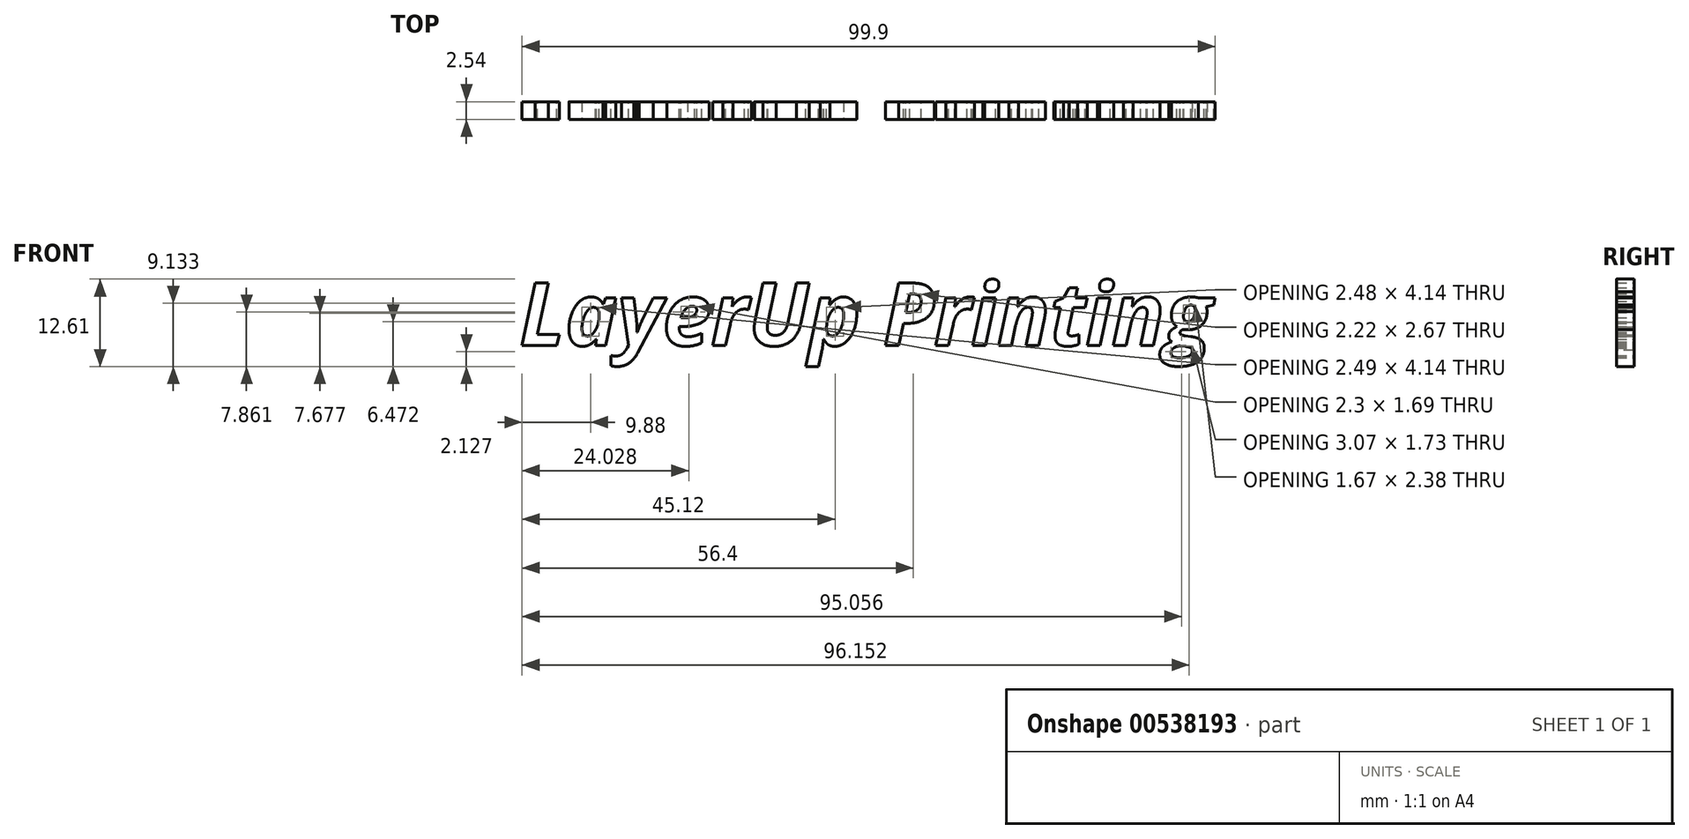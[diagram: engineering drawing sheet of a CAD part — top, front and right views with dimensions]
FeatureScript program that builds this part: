
annotation { "Feature Type Name" : "Feature", "Feature Type Description" : "" }
export const myFeature = defineFeature(function(context is Context, id is Id, definition is map)
    precondition{}
    {
        {
            var Q0;
            Q0=qCreatedBy(makeId("Front.planeOp"),FACE);
            var sketch = newSketch(context, id + "F0", { "sketchPlane" : qUnion([Q0])});
            skText(sketch, "E0", { "text": "LayerUp Printing", "fontName": "OpenSans-BoldItalic.ttf"});
            const initialGuessF0  = {"E0": [-0.06295, 0.01792, 1, 0, 0.00908]};
            skSetInitialGuess(sketch, initialGuessF0);
            skSolve(sketch);
        }
        {
            var Q0;
            Q0 = qSketchRegion(id + "F0", true);
            extrude(context, id + "F1", {"entities" : qUnion([Q0]), "depth" : 2.54 * mm, "offsetDistance" : 25.4 * mm});
        }
    });
